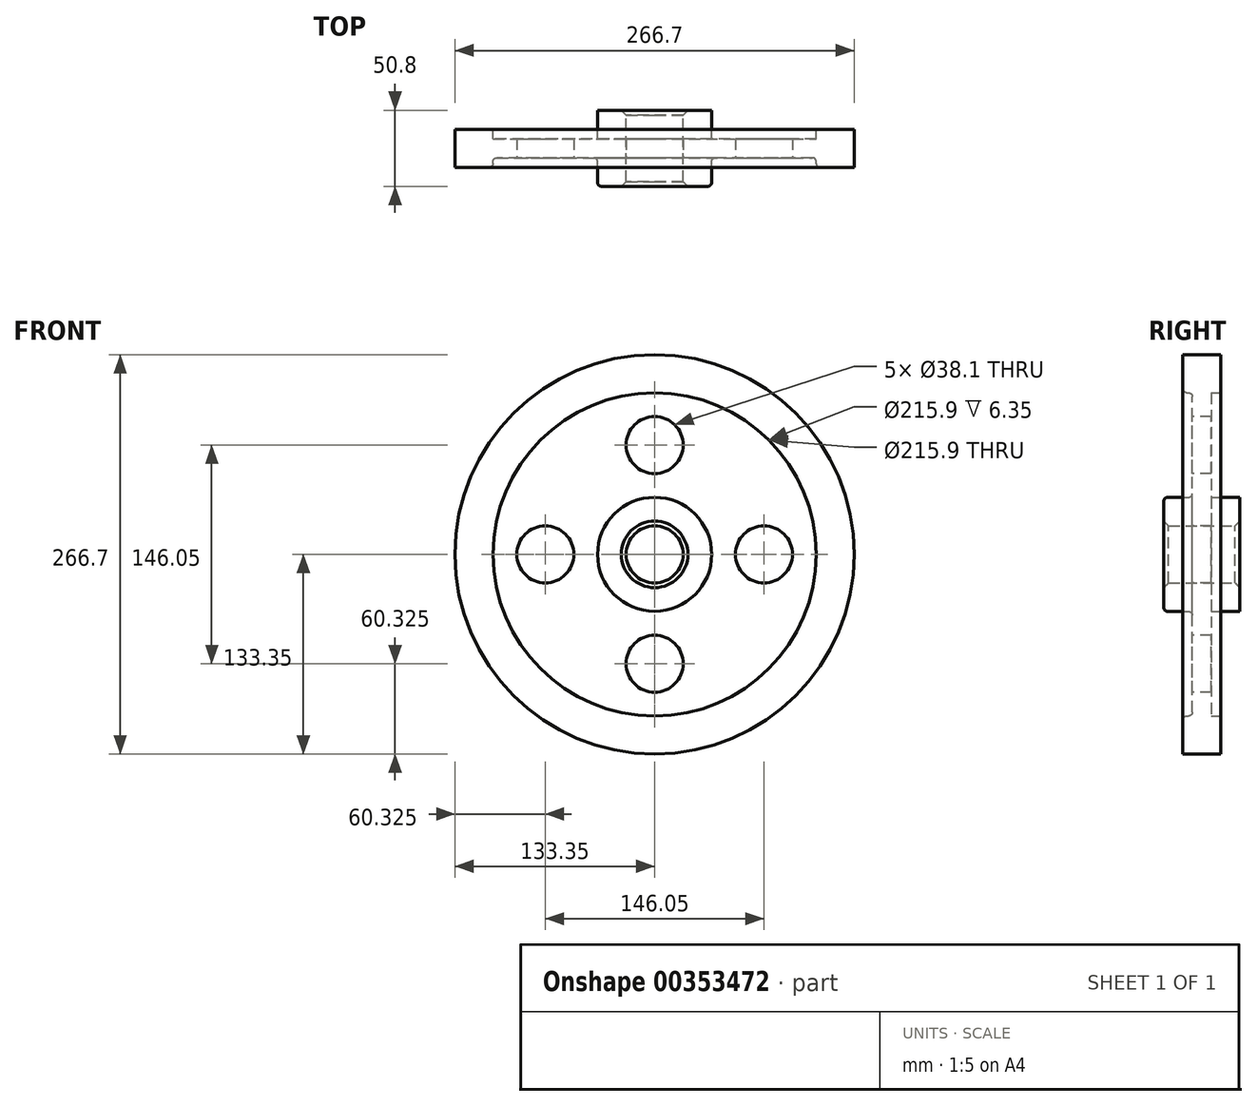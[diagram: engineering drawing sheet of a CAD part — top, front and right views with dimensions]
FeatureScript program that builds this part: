
annotation { "Feature Type Name" : "Feature", "Feature Type Description" : "" }
export const myFeature = defineFeature(function(context is Context, id is Id, definition is map)
    precondition{}
    {
        {
            var Q0;
            Q0=qCreatedBy(makeId("Right.planeOp"),FACE);
            var sketch = newSketch(context, id + "F0", { "sketchPlane" : qUnion([Q0])});
            skLineSegment(sketch, "E0", {"start": v(0, 0) * mm, "end": v(-59.37, 0) * mm, "construction": true});
            skLineSegment(sketch, "E1", {"start": v(0, 133.35) * mm, "end": v(0, 0) * mm, "construction": true});
            skLineSegment(sketch, "E2.MirrorCS", {"start": v(0, 19.05) * mm, "end": v(25.4, 19.05) * mm});
            skLineSegment(sketch, "E3.MirrorCS", {"start": v(6.35, 107.95) * mm, "end": v(12.7, 107.95) * mm});
            skLineSegment(sketch, "E4.MirrorCS", {"start": v(6.35, 107.95) * mm, "end": v(6.35, 38.1) * mm});
            skLineSegment(sketch, "E5.MirrorCS", {"start": v(6.35, 38.1) * mm, "end": v(25.4, 38.1) * mm});
            skLineSegment(sketch, "E6.MirrorCS", {"start": v(25.4, 38.1) * mm, "end": v(25.4, 19.05) * mm});
            skLineSegment(sketch, "E7.MirrorCS", {"start": v(12.7, 133.35) * mm, "end": v(12.7, 107.95) * mm});
            skLineSegment(sketch, "E8.MirrorCS", {"start": v(0, 133.35) * mm, "end": v(12.7, 133.35) * mm});
            skLineSegment(sketch, "E9.MirrorCS", {"start": v(-12.7, 133.35) * mm, "end": v(-12.7, 107.95) * mm});
            skLineSegment(sketch, "E10.MirrorCS", {"start": v(-6.35, 107.95) * mm, "end": v(-6.35, 38.1) * mm});
            skLineSegment(sketch, "E11.MirrorCS", {"start": v(-6.35, 38.1) * mm, "end": v(-25.4, 38.1) * mm});
            skLineSegment(sketch, "E12.MirrorCS", {"start": v(-25.4, 38.1) * mm, "end": v(-25.4, 19.05) * mm});
            skLineSegment(sketch, "E13.MirrorCS", {"start": v(0, 19.05) * mm, "end": v(-25.4, 19.05) * mm});
            skLineSegment(sketch, "E14.MirrorCS", {"start": v(0, 133.35) * mm, "end": v(-12.7, 133.35) * mm});
            skLineSegment(sketch, "E15.MirrorCS", {"start": v(-6.35, 107.95) * mm, "end": v(-12.7, 107.95) * mm});
            skSolve(sketch);
        }
        {
            var Q0;
            Q0=makeQuery(id+"F0.imprint","IMPRINT",FACE,{"disambiguationData":[TD([[makeQuery(id+"F0.imprint","IMPRINT",EDGE,{"derivedFrom":sQuery(id+"F0.wireOp",EDGE,"E2.MirrorCS")}),1.0]])]});
            var Q1;
            Q1=sQuery(id+"F0.wireOp",EDGE,"E0");
            revolve(context, id + "F1", {"entities" : qUnion([Q0]), "axis" : qUnion([Q1]), "revolveType" : RevolveType.FULL});
        }
        {
            var Q0;
            Q0=makeQuery(id+"F1.opRevolve","SWEPT_FACE",FACE,{"disambiguationData":[OSD([sQuery(id+"F0.wireOp",EDGE,"E10.MirrorCS")])]});
            var sketch = newSketch(context, id + "F2", { "sketchPlane" : qUnion([Q0])});
            skLineSegment(sketch, "E16", {"start": v(0, 0) * mm, "end": v(0, 73.03) * mm});
            skCircle(sketch, "E17", {"center": v(0, 73.03) * mm, "radius": 19.05 * mm});
            skCircle(sketch, "E18.1.0", {"center": v(-73.03, 0) * mm, "radius": 19.05 * mm});
            skCircle(sketch, "E18.2.0", {"center": v(0, -73.03) * mm, "radius": 19.05 * mm});
            skCircle(sketch, "E18.3.0", {"center": v(73.03, 0) * mm, "radius": 19.05 * mm});
            skPoint(sketch, "E18.center", {"position": v(0, 0) * mm});
            skSolve(sketch);
        }
        {
            var Q0;
            Q0=makeQuery(id+"F2.imprint","IMPRINT",FACE,{"disambiguationData":[TD([[makeQuery(id+"F2.imprint","IMPRINT",EDGE,{"derivedFrom":sQuery(id+"F2.wireOp",EDGE,"E18.1.0")}),1.0]])]});
            var Q1;
            Q1=makeQuery(id+"F2.imprint","IMPRINT",FACE,{"disambiguationData":[TD([[makeQuery(id+"F2.imprint","IMPRINT",EDGE,{"derivedFrom":sQuery(id+"F2.wireOp",EDGE,"E17")}),1.0]])]});
            var Q2;
            Q2=makeQuery(id+"F2.imprint","IMPRINT",FACE,{"disambiguationData":[TD([[makeQuery(id+"F2.imprint","IMPRINT",EDGE,{"derivedFrom":sQuery(id+"F2.wireOp",EDGE,"E18.3.0")}),1.0]])]});
            var Q3;
            Q3=makeQuery(id+"F2.imprint","IMPRINT",FACE,{"disambiguationData":[TD([[makeQuery(id+"F2.imprint","IMPRINT",EDGE,{"derivedFrom":sQuery(id+"F2.wireOp",EDGE,"E18.2.0")}),1.0]])]});
            extrude(context, id + "F3", {"entities" : qUnion([Q0, Q1, Q2, Q3]), "operationType" : NewBodyOperationType.REMOVE, "oppositeDirection" : true, "depth" : 25.4 * mm});
        }
        {
            var Q0;
            Q0=makeQuery(id+"F1.opRevolve","SWEPT_EDGE",EDGE,{"disambiguationData":[OSD([sQuery(id+"F0.wireOp",EDGE,"E10.MirrorCS"),sQuery(id+"F0.wireOp",EDGE,"E15.MirrorCS")])]});
            var Q1;
            Q1=makeQuery(id+"F1.opRevolve","SWEPT_EDGE",EDGE,{"disambiguationData":[OSD([sQuery(id+"F0.wireOp",EDGE,"E9.MirrorCS"),sQuery(id+"F0.wireOp",EDGE,"E15.MirrorCS")])]});
            var Q2;
            Q2=makeQuery(id+"F1.opRevolve","SWEPT_EDGE",EDGE,{"disambiguationData":[OSD([sQuery(id+"F0.wireOp",EDGE,"E11.MirrorCS"),sQuery(id+"F0.wireOp",EDGE,"E12.MirrorCS")])]});
            var Q3;
            Q3=makeQuery(id+"F1.opRevolve","SWEPT_FACE",FACE,{"disambiguationData":[OSD([sQuery(id+"F0.wireOp",EDGE,"E11.MirrorCS")])]});
            fillet(context, id + "F4", {"entities" : qUnion([Q0, Q1, Q2, Q3]), "radius" : 2.54 * mm, "tangentPropagation" : true, "allowEdgeOverflow" : false});
        }
        {
            var Q0;
            Q0=makeQuery(id+"F1.opRevolve","SWEPT_EDGE",EDGE,{"disambiguationData":[OSD([sQuery(id+"F0.wireOp",EDGE,"E12.MirrorCS"),sQuery(id+"F0.wireOp",EDGE,"E13.MirrorCS")])]});
            var Q1;
            Q1=makeQuery(id+"F1.opRevolve","SWEPT_EDGE",EDGE,{"disambiguationData":[OSD([sQuery(id+"F0.wireOp",EDGE,"E2.MirrorCS"),sQuery(id+"F0.wireOp",EDGE,"E6.MirrorCS")])]});
            chamfer(context, id + "F5", {"entities" : qUnion([Q0, Q1]), "width" : 3.17 * mm, "tangentPropagation" : true});
        }
    });
